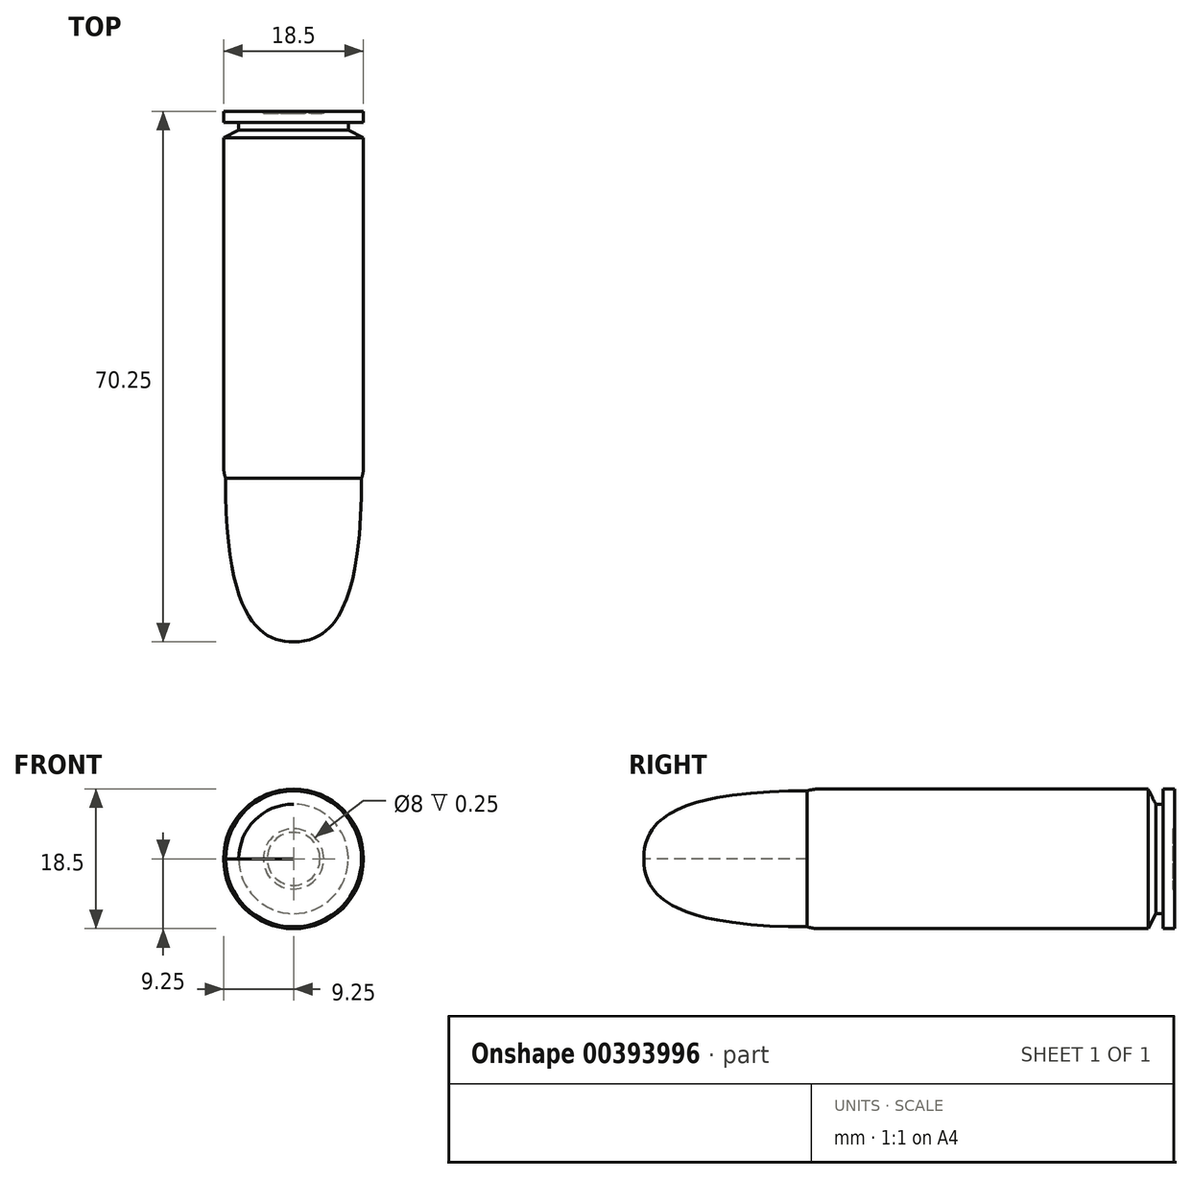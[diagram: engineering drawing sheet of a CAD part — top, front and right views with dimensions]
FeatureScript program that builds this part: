
annotation { "Feature Type Name" : "Feature", "Feature Type Description" : "" }
export const myFeature = defineFeature(function(context is Context, id is Id, definition is map)
    precondition{}
    {
        {
            var Q0;
            Q0=qCreatedBy(makeId("Top.planeOp"),FACE);
            var sketch = newSketch(context, id + "F0", { "sketchPlane" : qUnion([Q0])});
            skLineSegment(sketch, "E0.bottom", {"start": v(-9, 35) * mm, "end": v(9, 35) * mm});
            skLineSegment(sketch, "E0.top", {"start": v(-9, -35) * mm, "end": v(9, -35) * mm});
            skLineSegment(sketch, "E0.left", {"start": v(-9, 35) * mm, "end": v(-9, -13.38) * mm});
            skLineSegment(sketch, "E0.right", {"start": v(9, 35) * mm, "end": v(9, 0) * mm});
            skPoint(sketch, "E0.middle", {"position": v(0, 0) * mm});
            skLineSegment(sketch, "E1", {"start": v(0, 35.25) * mm, "end": v(0, -35) * mm});
            skFitSpline(sketch, "E2", {"points": [v(-9, -13.38) * mm, v(0, -35) * mm, v(9, -13.38) * mm], "startDerivative": vector(0, -111.73) * mm, "endDerivative": vector(0, 111.73) * mm});
            skLineSegment(sketch, "E3", {"start": v(-9, -13.38) * mm, "end": v(-9, -35) * mm});
            skLineSegment(sketch, "E4", {"start": v(9, 0) * mm, "end": v(9, -35) * mm});
            skLineSegment(sketch, "E5.0", {"start": v(-9.25, 35.25) * mm, "end": v(-9.25, -13.38) * mm});
            skLineSegment(sketch, "E5.1", {"start": v(-9.25, 35.25) * mm, "end": v(9, 35.25) * mm});
            skLineSegment(sketch, "E6", {"start": v(-9.25, -13.38) * mm, "end": v(-9, -13.38) * mm});
            skPoint(sketch, "E7.orphan", {"position": v(0, 35) * mm});
            skLineSegment(sketch, "E8", {"start": v(-9.25, 33.75) * mm, "end": v(-7.25, 33.75) * mm});
            skLineSegment(sketch, "E9", {"start": v(-7.25, 33.75) * mm, "end": v(-7.25, 32.75) * mm});
            skLineSegment(sketch, "E10", {"start": v(-7.25, 32.75) * mm, "end": v(-9.25, 31.75) * mm});
            skLineSegment(sketch, "E11", {"start": v(-4, 35.25) * mm, "end": v(-4, 35) * mm});
            skLineSegment(sketch, "E12", {"start": v(-3.5, 35) * mm, "end": v(-3.5, 35.25) * mm});
            skSolve(sketch);
        }
        {
            var Q0;
            {var subQ14=sQuery(id+"F0.wireOp",EDGE,"E9");Q0=makeQuery(id+"F0.imprint","IMPRINT",FACE,{"disambiguationData":[TD([[makeQuery(id+"F0.imprint","IMPRINT",EDGE,{"derivedFrom":subQ14}),1.0]])]});}
            var Q1;
            {var subQ9=sQuery(id+"F0.wireOp",EDGE,"E11");Q1=makeQuery(id+"F0.imprint","IMPRINT",FACE,{"disambiguationData":[TD([[makeQuery(id+"F0.imprint","IMPRINT",EDGE,{"derivedFrom":subQ9}),-1.0]])]});}
            var Q2;
            {var subQ0=sQuery(id+"F0.wireOp",EDGE,"E12");Q2=makeQuery(id+"F0.imprint","IMPRINT",FACE,{"disambiguationData":[TD([[makeQuery(id+"F0.imprint","IMPRINT",EDGE,{"derivedFrom":subQ0}),-1.0]])]});}
            var Q3;
            {var subQ0=sQuery(id+"F0.wireOp",EDGE,"E6");Q3=makeQuery(id+"F0.imprint","IMPRINT",FACE,{"disambiguationData":[TD([[makeQuery(id+"F0.imprint","IMPRINT",EDGE,{"derivedFrom":subQ0}),1.0]])]});}
            var Q4;
            Q4=sQuery(id+"F0.wireOp",EDGE,"E1");
            revolve(context, id + "F1", {"entities" : qUnion([Q0, Q1, Q2, Q3]), "axis" : qUnion([Q4]), "revolveType" : RevolveType.FULL});
        }
        {
            var Q0;
            Q0=makeQuery(id+"F1.opRevolve","SWEPT_EDGE",EDGE,{"disambiguationData":[OSD([sQuery(id+"F0.wireOp",EDGE,"E5.1"),sQuery(id+"F0.wireOp",EDGE,"E12")])]});
            fillet(context, id + "F2", {"entities" : qUnion([Q0]), "radius" : 0.5 * mm, "tangentPropagation" : true, "allowEdgeOverflow" : false});
        }
        {
            var Q0;
            Q0=makeQuery(id+"F1.opRevolve","SWEPT_EDGE",EDGE,{"disambiguationData":[OSD([sQuery(id+"F0.wireOp",EDGE,"E5.0"),sQuery(id+"F0.wireOp",EDGE,"E6")])]});
            fillet(context, id + "F3", {"entities" : qUnion([Q0]), "radius" : 5 * mm, "tangentPropagation" : true, "allowEdgeOverflow" : false});
        }
    });
